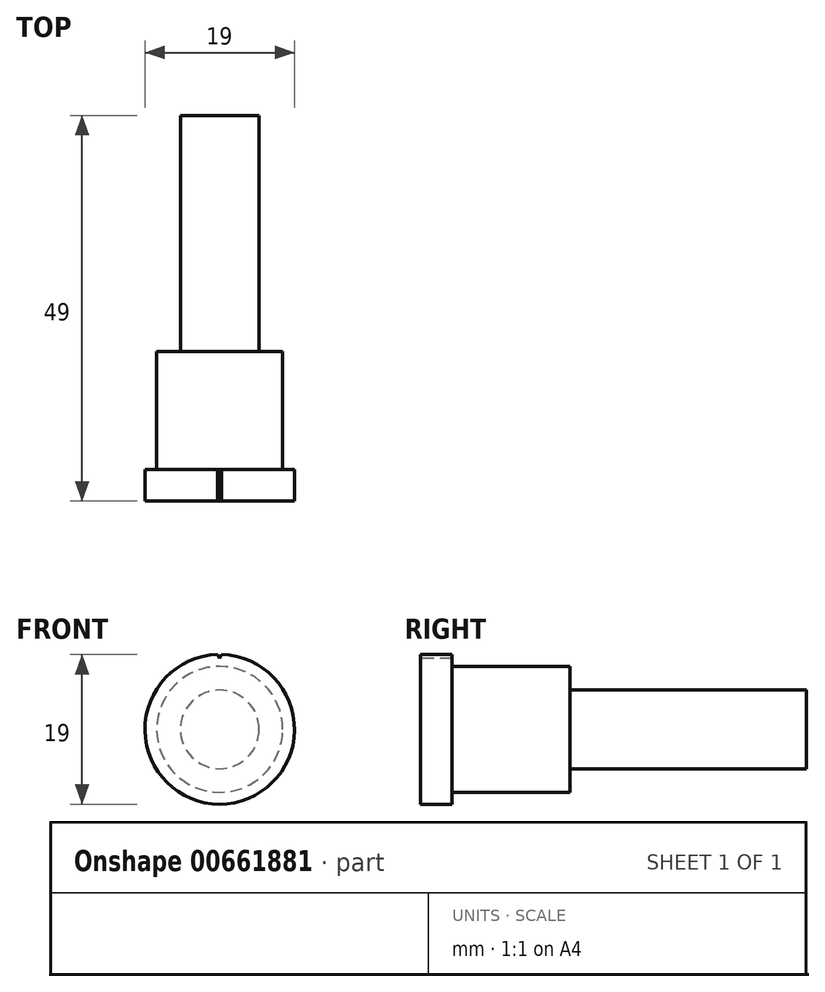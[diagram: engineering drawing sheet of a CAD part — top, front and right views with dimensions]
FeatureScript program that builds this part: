
annotation { "Feature Type Name" : "Feature", "Feature Type Description" : "" }
export const myFeature = defineFeature(function(context is Context, id is Id, definition is map)
    precondition{}
    {
        {
            var Q0;
            Q0=qCreatedBy(makeId("Right.planeOp"),FACE);
            var sketch = newSketch(context, id + "F0", { "sketchPlane" : qUnion([Q0])});
            skLineSegment(sketch, "E0", {"start": v(4, 8) * mm, "end": v(19, 8) * mm});
            skLineSegment(sketch, "E1", {"start": v(0, 9.5) * mm, "end": v(4, 9.5) * mm});
            skLineSegment(sketch, "E2", {"start": v(4, 9.5) * mm, "end": v(4, 8) * mm});
            skLineSegment(sketch, "E3", {"start": v(0, 0) * mm, "end": v(19, 0) * mm});
            skLineSegment(sketch, "E4", {"start": v(19, 5) * mm, "end": v(19, 8) * mm});
            skLineSegment(sketch, "E5", {"start": v(0, 9.5) * mm, "end": v(0, 0) * mm});
            skLineSegment(sketch, "E6", {"start": v(0, 0) * mm, "end": v(-15.8, 0) * mm, "construction": true});
            skLineSegment(sketch, "E7", {"start": v(19, 5) * mm, "end": v(49, 5) * mm});
            skLineSegment(sketch, "E8", {"start": v(49, 5) * mm, "end": v(49, 0) * mm});
            skLineSegment(sketch, "E9", {"start": v(19, 0) * mm, "end": v(49, 0) * mm});
            skSolve(sketch);
        }
        {
            var Q0;
            Q0 = qSketchRegion(id + "F0", true);
            var Q1;
            Q1=sQuery(id+"F0.wireOp",EDGE,"E6");
            revolve(context, id + "F1", {"surfaceOperationType" : NewSurfaceOperationType.NEW, "entities" : qUnion([Q0]), "axis" : qUnion([Q1]), "revolveType" : RevolveType.FULL});
        }
        {
            var Q0;
            Q0=makeQuery(id+"F1.opRevolve","SWEPT_FACE",FACE,{"disambiguationData":[OSD([sQuery(id+"F0.wireOp",EDGE,"E5")])]});
            var sketch = newSketch(context, id + "F2", { "sketchPlane" : qUnion([Q0])});
            skLineSegment(sketch, "E10", {"start": v(0, 0) * mm, "end": v(0, 9.5) * mm, "construction": true});
            skLineSegment(sketch, "E11", {"start": v(-0.25, 9.5) * mm, "end": v(0, 9) * mm});
            skLineSegment(sketch, "E12", {"start": v(0, 9) * mm, "end": v(0.25, 9.5) * mm});
            skArc(sketch, "E13", {"start": v(0.25, 9.5) * mm, "mid": v(0, 9.75) * mm, "end": v(-0.25, 9.5) * mm});
            skSolve(sketch);
        }
        {
            var Q0;
            Q0 = qSketchRegion(id + "F2", true);
            extrude(context, id + "F3", {"entities" : qUnion([Q0]), "operationType" : NewBodyOperationType.REMOVE, "endBound" : BoundingType.UP_TO_NEXT, "oppositeDirection" : true, "depth" : 25 * mm, "offsetDistance" : 25 * mm});
        }
    });
